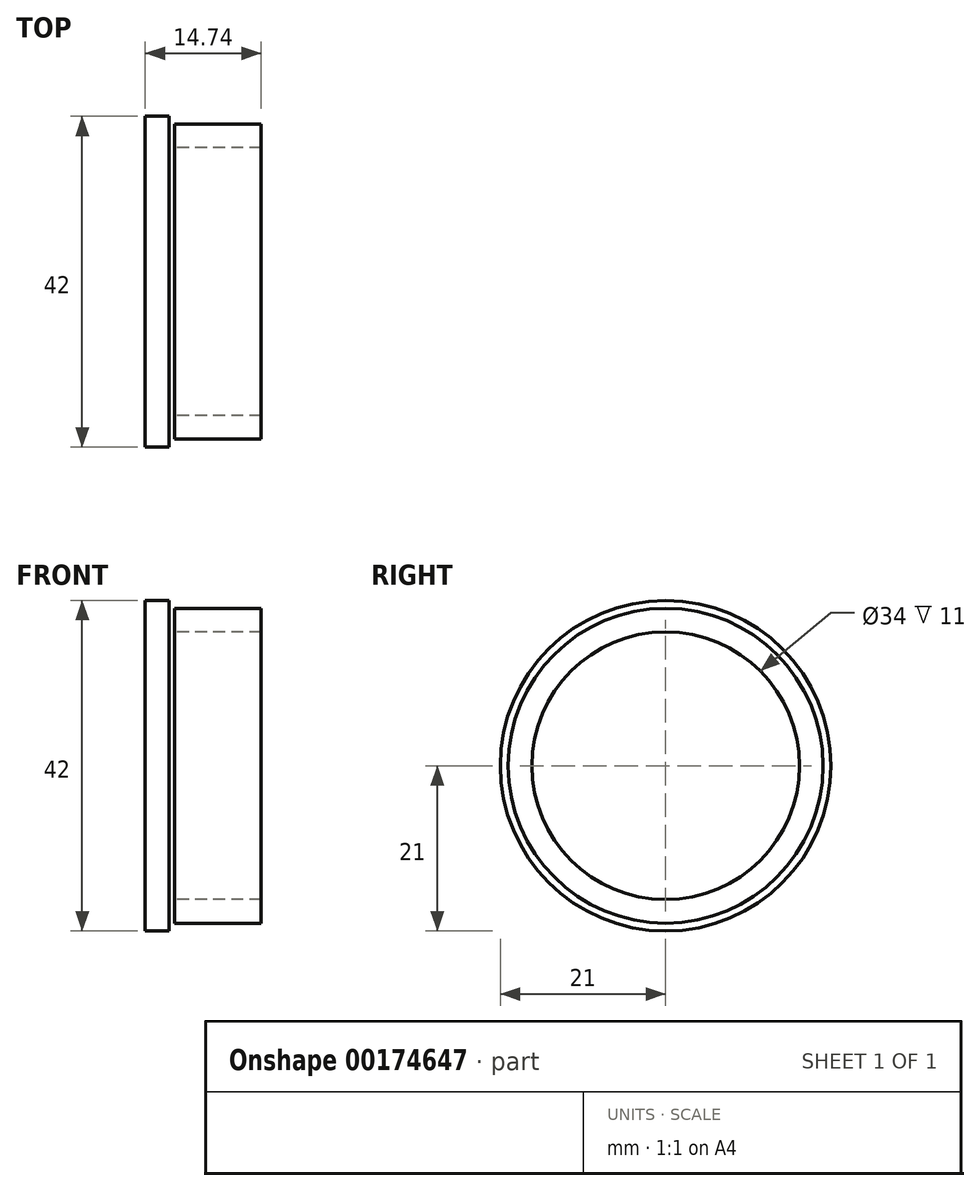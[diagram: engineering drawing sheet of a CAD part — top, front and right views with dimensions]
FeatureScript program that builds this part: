
annotation { "Feature Type Name" : "Feature", "Feature Type Description" : "" }
export const myFeature = defineFeature(function(context is Context, id is Id, definition is map)
    precondition{}
    {
        {
            var Q0;
            Q0=qCreatedBy(makeId("Front.planeOp"),FACE);
            var sketch = newSketch(context, id + "F0", { "sketchPlane" : qUnion([Q0])});
            skLineSegment(sketch, "E0.bottom", {"start": v(0, 0) * mm, "end": v(3, 0) * mm});
            skLineSegment(sketch, "E0.top", {"start": v(0, 21) * mm, "end": v(3, 21) * mm});
            skLineSegment(sketch, "E0.left", {"start": v(0, 0) * mm, "end": v(0, 21) * mm});
            skLineSegment(sketch, "E0.right", {"start": v(3, 0) * mm, "end": v(3, 21) * mm});
            skSolve(sketch);
        }
        {
            var Q0;
            Q0 = qSketchRegion(id + "F0", true);
            var Q1;
            Q1=sQuery(id+"F0.wireOp",EDGE,"E0.bottom");
            revolve(context, id + "F1", {"entities" : qUnion([Q0]), "axis" : qUnion([Q1]), "revolveType" : RevolveType.FULL});
        }
        {
            var Q0;
            Q0=qCreatedBy(makeId("Front.planeOp"),FACE);
            var sketch = newSketch(context, id + "F2", { "sketchPlane" : qUnion([Q0])});
            skPoint(sketch, "E1.bottom.start.orphan", {"position": v(2.15, 0) * mm});
            skLineSegment(sketch, "E2.bottom", {"start": v(3.74, 0) * mm, "end": v(14.74, 0) * mm});
            skLineSegment(sketch, "E2.top", {"start": v(3.74, 17) * mm, "end": v(14.74, 17) * mm});
            skLineSegment(sketch, "E2.left", {"start": v(3.74, 0) * mm, "end": v(3.74, 17) * mm});
            skLineSegment(sketch, "E2.right", {"start": v(14.74, 0) * mm, "end": v(14.74, 17) * mm});
            skLineSegment(sketch, "E3.top", {"start": v(3.74, 20) * mm, "end": v(14.74, 20) * mm});
            skLineSegment(sketch, "E3.left", {"start": v(3.74, 0) * mm, "end": v(3.74, 20) * mm});
            skLineSegment(sketch, "E3.right", {"start": v(14.74, 0) * mm, "end": v(14.74, 20) * mm});
            skSolve(sketch);
        }
        {
            var Q0;
            {var subQ0=sQuery(id+"F2.wireOp",EDGE,"E2.top");Q0=makeQuery(id+"F2.imprint","IMPRINT",FACE,{"disambiguationData":[TD([[makeQuery(id+"F2.imprint","IMPRINT",EDGE,{"derivedFrom":subQ0}),1.0]])]});}
            var Q1;
            Q1=sQuery(id+"F2.wireOp",EDGE,"E2.bottom");
            revolve(context, id + "F3", {"entities" : qUnion([Q0]), "axis" : qUnion([Q1]), "revolveType" : RevolveType.FULL});
        }
    });
